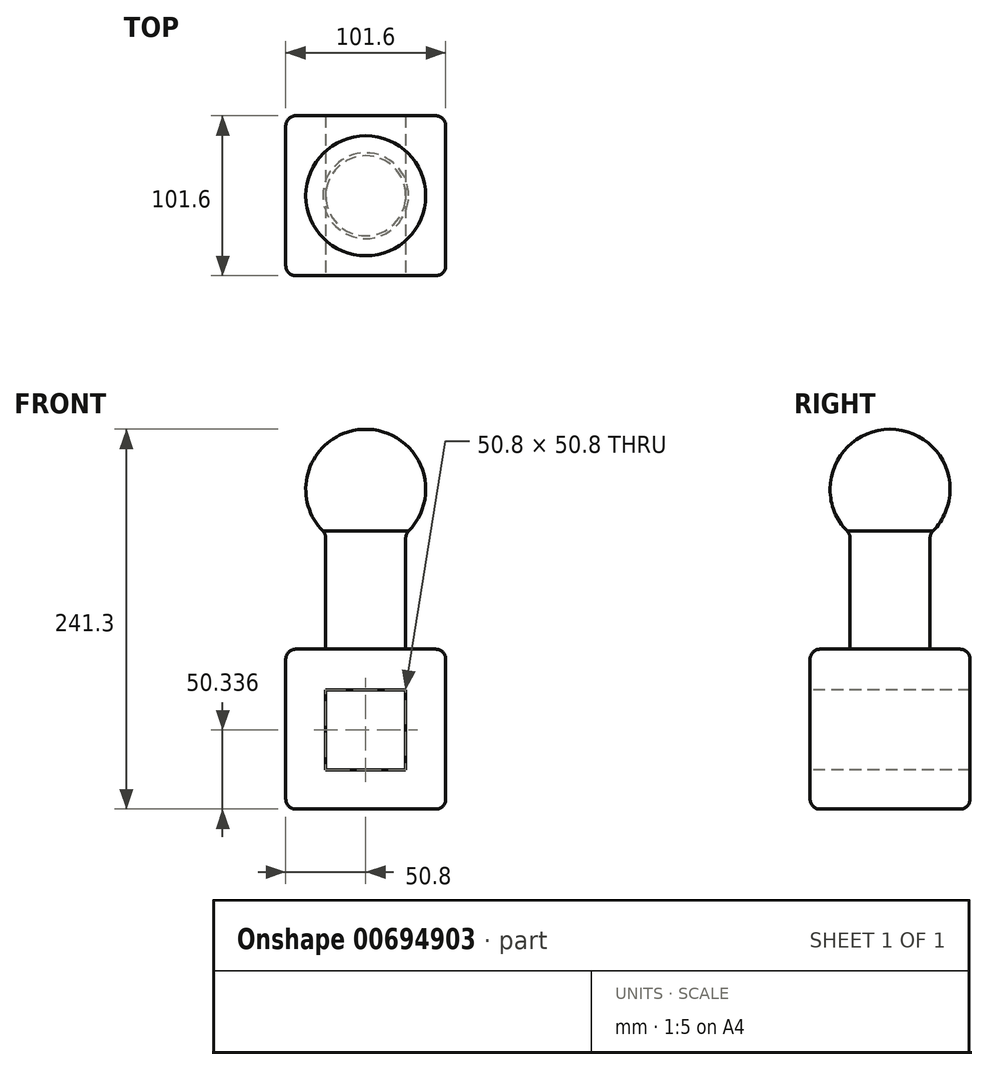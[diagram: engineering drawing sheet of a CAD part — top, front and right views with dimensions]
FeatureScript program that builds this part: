
annotation { "Feature Type Name" : "Feature", "Feature Type Description" : "" }
export const myFeature = defineFeature(function(context is Context, id is Id, definition is map)
    precondition{}
    {
        {
            var Q0;
            Q0=qCreatedBy(makeId("Top.planeOp"),FACE);
            var sketch = newSketch(context, id + "F0", { "sketchPlane" : qUnion([Q0])});
            skLineSegment(sketch, "E0.bottom", {"start": v(50.8, -50.8) * mm, "end": v(-50.8, -50.8) * mm});
            skLineSegment(sketch, "E0.top", {"start": v(50.8, 50.8) * mm, "end": v(-50.8, 50.8) * mm});
            skLineSegment(sketch, "E0.left", {"start": v(50.8, -50.8) * mm, "end": v(50.8, 50.8) * mm});
            skLineSegment(sketch, "E0.right", {"start": v(-50.8, -50.8) * mm, "end": v(-50.8, 50.8) * mm});
            skPoint(sketch, "E0.middle", {"position": v(0, 0) * mm});
            skSolve(sketch);
        }
        {
            var Q0;
            Q0 = qSketchRegion(id + "F0", true);
            extrude(context, id + "F1", {"entities" : qUnion([Q0]), "depth" : 101.6 * mm, "offsetDistance" : 25.4 * mm});
        }
        {
            var Q0;
            Q0=makeQuery(id+"F1.opExtrude","CAP_FACE",FACE,{"disambiguationData":[OSD([sQuery(id+"F0.wireOp",EDGE,"E0.bottom"),sQuery(id+"F0.wireOp",EDGE,"E0.top"),sQuery(id+"F0.wireOp",EDGE,"E0.left"),sQuery(id+"F0.wireOp",EDGE,"E0.right")])],"isStart":false});
            var sketch = newSketch(context, id + "F2", { "sketchPlane" : qUnion([Q0])});
            skCircle(sketch, "E1", {"center": v(0, 0) * mm, "radius": 25.4 * mm});
            skSolve(sketch);
        }
        {
            var Q0;
            Q0=makeQuery(id+"F2.imprint","IMPRINT",FACE,{"disambiguationData":[TD([[makeQuery(id+"F2.imprint","IMPRINT",EDGE,{"derivedFrom":sQuery(id+"F2.wireOp",EDGE,"E1")}),1.0]])]});
            extrude(context, id + "F3", {"entities" : qUnion([Q0]), "operationType" : NewBodyOperationType.ADD, "depth" : 101.6 * mm, "offsetDistance" : 25.4 * mm});
        }
        {
            var Q0;
            Q0=makeQuery(id+"F3.opExtrude","CAP_FACE",FACE,{"disambiguationData":[OSD([sQuery(id+"F2.wireOp",EDGE,"E1")])],"isStart":false});
            var sketch = newSketch(context, id + "F4", { "sketchPlane" : qUnion([Q0])});
            skArc(sketch, "E2", {"start": v(0, -38.1) * mm, "mid": v(38.1, 0) * mm, "end": v(0, 38.1) * mm});
            skLineSegment(sketch, "E3", {"start": v(0, 38.1) * mm, "end": v(0, -38.1) * mm});
            skSolve(sketch);
        }
        {
            var Q0;
            {var subQ0=sQuery(id+"F4.wireOp",EDGE,"E2");Q0=makeQuery(id+"F4.imprint","IMPRINT",FACE,{"disambiguationData":[TD([[makeQuery(id+"F4.imprint","IMPRINT",EDGE,{"derivedFrom":subQ0}),1.0]])]});}
            var Q1;
            {var subQ0=sQuery(id+"F4.wireOp",EDGE,"E3");var subQ1=makeQuery(id+"F3.opExtrude","CAP_EDGE",EDGE,{"disambiguationData":[OSD([sQuery(id+"F2.wireOp",EDGE,"E1")])],"isStart":false});var subQ2=makeQuery(id+"F4.imprint","INTERSECT",VERTEX,{"disambiguationData":[OD(0.0)],"derivedFrom":[subQ1,subQ0]});Q1=makeQuery(id+"F4.imprint","IMPRINT",FACE,{"disambiguationData":[TD([[makeQuery(id+"F4.imprint","IMPRINT",EDGE,{"disambiguationData":[TD([[subQ2,-1.0]])],"derivedFrom":subQ0}),1.0]])]});}
            var Q2;
            Q2=sQuery(id+"F4.wireOp",EDGE,"E3");
            revolve(context, id + "F5", {"operationType" : NewBodyOperationType.ADD, "entities" : qUnion([Q0, Q1]), "axis" : qUnion([Q2]), "revolveType" : RevolveType.FULL});
        }
        {
            var Q0;
            Q0=makeQuery(id+"F1.opExtrude","SWEPT_FACE",FACE,{"disambiguationData":[OSD([sQuery(id+"F0.wireOp",EDGE,"E0.bottom")])]});
            var sketch = newSketch(context, id + "F6", { "sketchPlane" : qUnion([Q0])});
            skLineSegment(sketch, "E4.bottom", {"start": v(25.4, 75.74) * mm, "end": v(-25.4, 75.74) * mm});
            skLineSegment(sketch, "E4.top", {"start": v(25.4, 24.94) * mm, "end": v(-25.4, 24.94) * mm});
            skLineSegment(sketch, "E4.left", {"start": v(25.4, 75.74) * mm, "end": v(25.4, 24.94) * mm});
            skLineSegment(sketch, "E4.right", {"start": v(-25.4, 75.74) * mm, "end": v(-25.4, 24.94) * mm});
            skPoint(sketch, "E4.middle", {"position": v(0, 50.34) * mm});
            skSolve(sketch);
        }
        {
            var Q0;
            Q0=makeQuery(id+"F6.imprint","IMPRINT",FACE,{"disambiguationData":[TD([[makeQuery(id+"F6.imprint","IMPRINT",EDGE,{"derivedFrom":sQuery(id+"F6.wireOp",EDGE,"E4.bottom")}),1.0]])]});
            extrude(context, id + "F7", {"entities" : qUnion([Q0]), "operationType" : NewBodyOperationType.REMOVE, "oppositeDirection" : true, "depth" : 101.6 * mm, "offsetDistance" : 25.4 * mm});
        }
        {
            var Q0;
            Q0=makeQuery(id+"F1.opExtrude","SWEPT_EDGE",EDGE,{"disambiguationData":[OSD([sQuery(id+"F0.wireOp",EDGE,"E0.bottom"),sQuery(id+"F0.wireOp",EDGE,"E0.left")])]});
            var Q1;
            Q1=makeQuery(id+"F1.opExtrude","CAP_EDGE",EDGE,{"disambiguationData":[OSD([sQuery(id+"F0.wireOp",EDGE,"E0.left")])],"isStart":false});
            var Q2;
            Q2=makeQuery(id+"F1.opExtrude","CAP_EDGE",EDGE,{"disambiguationData":[OSD([sQuery(id+"F0.wireOp",EDGE,"E0.left")])],"isStart":true});
            var Q3;
            Q3=makeQuery(id+"F1.opExtrude","SWEPT_EDGE",EDGE,{"disambiguationData":[OSD([sQuery(id+"F0.wireOp",EDGE,"E0.top"),sQuery(id+"F0.wireOp",EDGE,"E0.left")])]});
            var Q4;
            Q4=makeQuery(id+"F1.opExtrude","CAP_EDGE",EDGE,{"disambiguationData":[OSD([sQuery(id+"F0.wireOp",EDGE,"E0.right")])],"isStart":false});
            var Q5;
            Q5=makeQuery(id+"F1.opExtrude","CAP_EDGE",EDGE,{"disambiguationData":[OSD([sQuery(id+"F0.wireOp",EDGE,"E0.bottom")])],"isStart":false});
            var Q6;
            Q6=makeQuery(id+"F1.opExtrude","SWEPT_EDGE",EDGE,{"disambiguationData":[OSD([sQuery(id+"F0.wireOp",EDGE,"E0.bottom"),sQuery(id+"F0.wireOp",EDGE,"E0.right")])]});
            var Q7;
            Q7=makeQuery(id+"F1.opExtrude","CAP_EDGE",EDGE,{"disambiguationData":[OSD([sQuery(id+"F0.wireOp",EDGE,"E0.top")])],"isStart":false});
            var Q8;
            Q8=makeQuery(id+"F1.opExtrude","CAP_EDGE",EDGE,{"disambiguationData":[OSD([sQuery(id+"F0.wireOp",EDGE,"E0.bottom")])],"isStart":true});
            var Q9;
            Q9=makeQuery(id+"F1.opExtrude","CAP_FACE",FACE,{"disambiguationData":[OSD([sQuery(id+"F0.wireOp",EDGE,"E0.bottom"),sQuery(id+"F0.wireOp",EDGE,"E0.top"),sQuery(id+"F0.wireOp",EDGE,"E0.left"),sQuery(id+"F0.wireOp",EDGE,"E0.right")])],"isStart":true});
            var Q10;
            Q10=makeQuery(id+"F1.opExtrude","SWEPT_EDGE",EDGE,{"disambiguationData":[OSD([sQuery(id+"F0.wireOp",EDGE,"E0.top"),sQuery(id+"F0.wireOp",EDGE,"E0.right")])]});
            var Q11;
            Q11=makeQuery(id+"F1.opExtrude","CAP_EDGE",EDGE,{"disambiguationData":[OSD([sQuery(id+"F0.wireOp",EDGE,"E0.top")])],"isStart":true});
            var Q12;
            Q12=makeQuery(id+"F3.opExtrude","CAP_EDGE",EDGE,{"disambiguationData":[OSD([sQuery(id+"F2.wireOp",EDGE,"E1")])],"isStart":true});
            var Q13;
            Q13=makeQuery(id+"F5.boolean.opBoolean","INTERSECT",EDGE,{"derivedFrom":[makeQuery(id+"F3.opExtrude","SWEPT_FACE",FACE,{"disambiguationData":[OSD([sQuery(id+"F2.wireOp",EDGE,"E1")])]}),makeQuery(id+"F5.opRevolve","SWEPT_FACE",FACE,{"disambiguationData":[OSD([sQuery(id+"F4.wireOp",EDGE,"E2")])]})]});
            fillet(context, id + "F8", {"entities" : qUnion([Q0, Q1, Q2, Q3, Q4, Q5, Q6, Q7, Q8, Q9, Q10, Q11, Q12, Q13]), "radius" : 6.35 * mm, "tangentPropagation" : true, "allowEdgeOverflow" : false});
        }
    });
